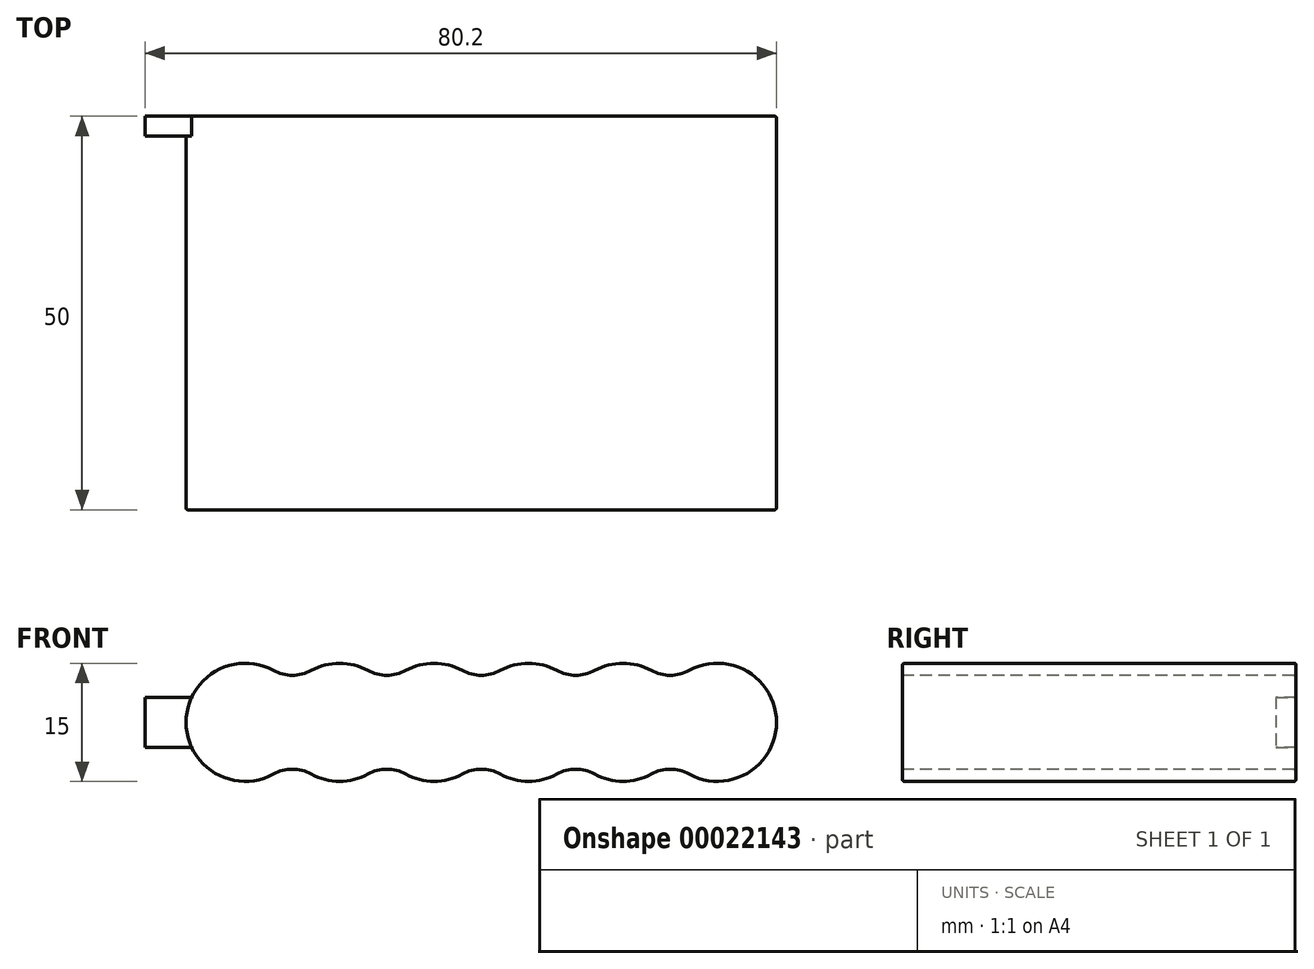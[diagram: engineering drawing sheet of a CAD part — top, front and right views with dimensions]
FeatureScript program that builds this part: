
annotation { "Feature Type Name" : "Feature", "Feature Type Description" : "" }
export const myFeature = defineFeature(function(context is Context, id is Id, definition is map)
    precondition{}
    {
        {
            var Q0;
            Q0=qCreatedBy(makeId("Front.planeOp"),FACE);
            var sketch = newSketch(context, id + "F0", { "sketchPlane" : qUnion([Q0])});
            skArc(sketch, "E0", {"start": v(6, 4.5) * mm, "mid": v(-7.5, 0) * mm, "end": v(6, -4.5) * mm});
            skArc(sketch, "E1.1.0.0", {"start": v(6, -4.5) * mm, "mid": v(12, -7.5) * mm, "end": v(18, -4.5) * mm});
            skArc(sketch, "E1.2.0.0", {"start": v(18, -4.5) * mm, "mid": v(24, -7.5) * mm, "end": v(30, -4.5) * mm});
            skArc(sketch, "E1.3.0.0", {"start": v(30, -4.5) * mm, "mid": v(36, -7.5) * mm, "end": v(42, -4.5) * mm});
            skArc(sketch, "E1.4.0.0", {"start": v(42, -4.5) * mm, "mid": v(48, -7.5) * mm, "end": v(54, -4.5) * mm});
            skArc(sketch, "E1.5.0.0", {"start": v(54, -4.5) * mm, "mid": v(67.5, 0) * mm, "end": v(54, 4.5) * mm});
            skLineSegment(sketch, "E1.direction1", {"start": v(0, 0) * mm, "end": v(12, 0) * mm, "construction": true});
            skArc(sketch, "E2.trimOffspring", {"start": v(18, 4.5) * mm, "mid": v(12, 7.5) * mm, "end": v(6, 4.5) * mm});
            skArc(sketch, "E3.trimOffspring", {"start": v(30, 4.5) * mm, "mid": v(24, 7.5) * mm, "end": v(18, 4.5) * mm});
            skArc(sketch, "E4.trimOffspring", {"start": v(42, 4.5) * mm, "mid": v(36, 7.5) * mm, "end": v(30, 4.5) * mm});
            skArc(sketch, "E5.trimOffspring", {"start": v(54, 4.5) * mm, "mid": v(48, 7.5) * mm, "end": v(42, 4.5) * mm});
            skSolve(sketch);
        }
        {
            var Q0;
            Q0 = qSketchRegion(id + "F0", true);
            extrude(context, id + "F1", {"entities" : qUnion([Q0]), "depth" : 50 * mm});
        }
        {
            var Q0;
            Q0=qCreatedBy(makeId("Right.planeOp"),FACE);
            var sketch = newSketch(context, id + "F2", { "sketchPlane" : qUnion([Q0])});
            skLineSegment(sketch, "E6.bottom", {"start": v(0, 3.17) * mm, "end": v(-2.54, 3.17) * mm});
            skLineSegment(sketch, "E6.top", {"start": v(0, -3.17) * mm, "end": v(-2.54, -3.17) * mm});
            skLineSegment(sketch, "E6.left", {"start": v(0, 3.17) * mm, "end": v(0, -3.17) * mm});
            skLineSegment(sketch, "E6.right", {"start": v(-2.54, 3.17) * mm, "end": v(-2.54, -3.17) * mm});
            skSolve(sketch);
        }
        {
            var Q0;
            Q0 = qSketchRegion(id + "F2", true);
            extrude(context, id + "F3", {"entities" : qUnion([Q0]), "operationType" : NewBodyOperationType.ADD, "oppositeDirection" : true, "depth" : 12.7 * mm});
        }
        {
            var Q0;
            Q0=makeQuery(id+"F1.opExtrude","SWEPT_EDGE",EDGE,{"disambiguationData":[OSD([sQuery(id+"F0.wireOp",EDGE,"E0"),sQuery(id+"F0.wireOp",EDGE,"E2.trimOffspring")])]});
            var Q1;
            Q1=makeQuery(id+"F1.opExtrude","SWEPT_EDGE",EDGE,{"disambiguationData":[OSD([sQuery(id+"F0.wireOp",EDGE,"E2.trimOffspring"),sQuery(id+"F0.wireOp",EDGE,"E3.trimOffspring")])]});
            var Q2;
            Q2=makeQuery(id+"F1.opExtrude","SWEPT_EDGE",EDGE,{"disambiguationData":[OSD([sQuery(id+"F0.wireOp",EDGE,"E3.trimOffspring"),sQuery(id+"F0.wireOp",EDGE,"E4.trimOffspring")])]});
            var Q3;
            Q3=makeQuery(id+"F1.opExtrude","SWEPT_EDGE",EDGE,{"disambiguationData":[OSD([sQuery(id+"F0.wireOp",EDGE,"E4.trimOffspring"),sQuery(id+"F0.wireOp",EDGE,"E5.trimOffspring")])]});
            var Q4;
            Q4=makeQuery(id+"F1.opExtrude","SWEPT_EDGE",EDGE,{"disambiguationData":[OSD([sQuery(id+"F0.wireOp",EDGE,"E1.5.0.0"),sQuery(id+"F0.wireOp",EDGE,"E5.trimOffspring")])]});
            var Q5;
            Q5=makeQuery(id+"F1.opExtrude","SWEPT_EDGE",EDGE,{"disambiguationData":[OSD([sQuery(id+"F0.wireOp",EDGE,"E1.4.0.0"),sQuery(id+"F0.wireOp",EDGE,"E1.5.0.0")])]});
            var Q6;
            Q6=makeQuery(id+"F1.opExtrude","SWEPT_EDGE",EDGE,{"disambiguationData":[OSD([sQuery(id+"F0.wireOp",EDGE,"E1.3.0.0"),sQuery(id+"F0.wireOp",EDGE,"E1.4.0.0")])]});
            var Q7;
            Q7=makeQuery(id+"F1.opExtrude","SWEPT_EDGE",EDGE,{"disambiguationData":[OSD([sQuery(id+"F0.wireOp",EDGE,"E1.2.0.0"),sQuery(id+"F0.wireOp",EDGE,"E1.3.0.0")])]});
            var Q8;
            Q8=makeQuery(id+"F1.opExtrude","SWEPT_EDGE",EDGE,{"disambiguationData":[OSD([sQuery(id+"F0.wireOp",EDGE,"E1.1.0.0"),sQuery(id+"F0.wireOp",EDGE,"E1.2.0.0")])]});
            var Q9;
            Q9=makeQuery(id+"F1.opExtrude","SWEPT_EDGE",EDGE,{"disambiguationData":[OSD([sQuery(id+"F0.wireOp",EDGE,"E0"),sQuery(id+"F0.wireOp",EDGE,"E1.1.0.0")])]});
            fillet(context, id + "F4", {"entities" : qUnion([Q0, Q1, Q2, Q3, Q4, Q5, Q6, Q7, Q8, Q9]), "radius" : 5 * mm, "tangentPropagation" : true, "allowEdgeOverflow" : false});
        }
        {
            var Q0;
            Q0=makeQuery(id+"F1.opExtrude","CAP_EDGE",EDGE,{"disambiguationData":[OSD([sQuery(id+"F0.wireOp",EDGE,"E0")])],"isStart":false});
            var Q1;
            Q1=makeQuery(id+"F1.opExtrude","CAP_EDGE",EDGE,{"disambiguationData":[OSD([sQuery(id+"F0.wireOp",EDGE,"E1.2.0.0")])],"isStart":true});
            fillet(context, id + "F5", {"entities" : qUnion([Q0, Q1]), "radius" : .25 * mm, "tangentPropagation" : true, "allowEdgeOverflow" : false});
        }
    });
